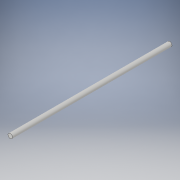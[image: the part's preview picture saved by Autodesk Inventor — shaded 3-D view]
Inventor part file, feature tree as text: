
AUTODESK INVENTOR PART (.ipt)
format: ipt  version: 2019 (Build 230136000, 136)  size: 95,232 bytes
history: native  units: mm
features: other x1, extrude x1, sketch x1
ambient origin geometry x8: Origin, YZ Plane, XZ Plane, XY Plane, X Axis, Y Axis, Z Axis, Center Point
bodies: Body1 (feature_tree)
feature tree (3):
  other  "ソリッド1"
  extrude  "押し出し1"  Depth=2.0mm
  sketch  "スケッチ1"
